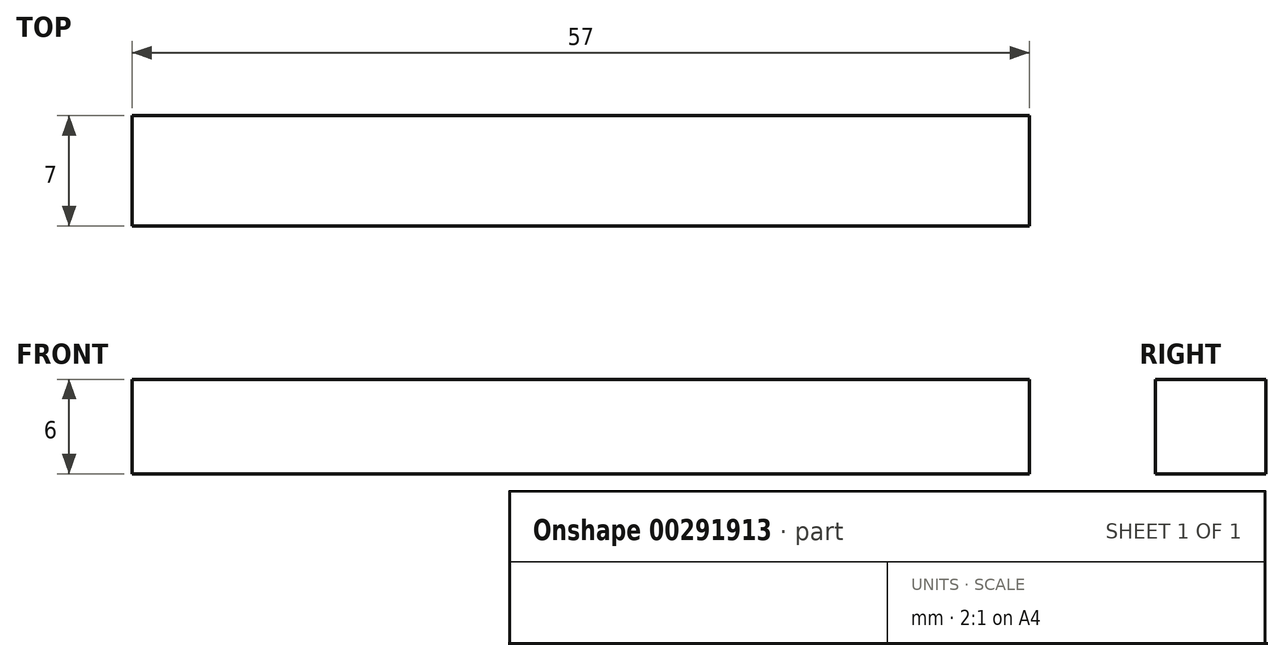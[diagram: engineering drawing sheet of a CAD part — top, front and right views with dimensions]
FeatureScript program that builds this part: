
annotation { "Feature Type Name" : "Feature", "Feature Type Description" : "" }
export const myFeature = defineFeature(function(context is Context, id is Id, definition is map)
    precondition{}
    {
        {
            var Q0;
            Q0=qCreatedBy(makeId("Front.planeOp"),FACE);
            var sketch = newSketch(context, id + "F0", { "sketchPlane" : qUnion([Q0])});
            skLineSegment(sketch, "E0", {"start": v(0, 3) * mm, "end": v(28.5, 3) * mm});
            skLineSegment(sketch, "E1", {"start": v(28.5, 3) * mm, "end": v(28.5, 0) * mm});
            skLineSegment(sketch, "E2.MirrorCS", {"start": v(0, -3) * mm, "end": v(28.5, -3) * mm});
            skLineSegment(sketch, "E3.MirrorCS", {"start": v(28.5, -3) * mm, "end": v(28.5, 0) * mm});
            skLineSegment(sketch, "E4.MirrorCS", {"start": v(-28.5, -3) * mm, "end": v(-28.5, 0) * mm});
            skLineSegment(sketch, "E5.MirrorCS", {"start": v(-28.5, 3) * mm, "end": v(-28.5, 0) * mm});
            skLineSegment(sketch, "E6.MirrorCS", {"start": v(0, -3) * mm, "end": v(-28.5, -3) * mm});
            skLineSegment(sketch, "E7.MirrorCS", {"start": v(0, 3) * mm, "end": v(-28.5, 3) * mm});
            skSolve(sketch);
        }
        {
            var Q0;
            Q0=makeQuery(id+"F0.imprint","IMPRINT",FACE,{"disambiguationData":[TD([[makeQuery(id+"F0.imprint","IMPRINT",EDGE,{"derivedFrom":sQuery(id+"F0.wireOp",EDGE,"E0")}),-1.0]])]});
            extrude(context, id + "F1", {"entities" : qUnion([Q0]), "endBound" : BoundingType.SYMMETRIC, "depth" : 7 * mm});
        }
    });
